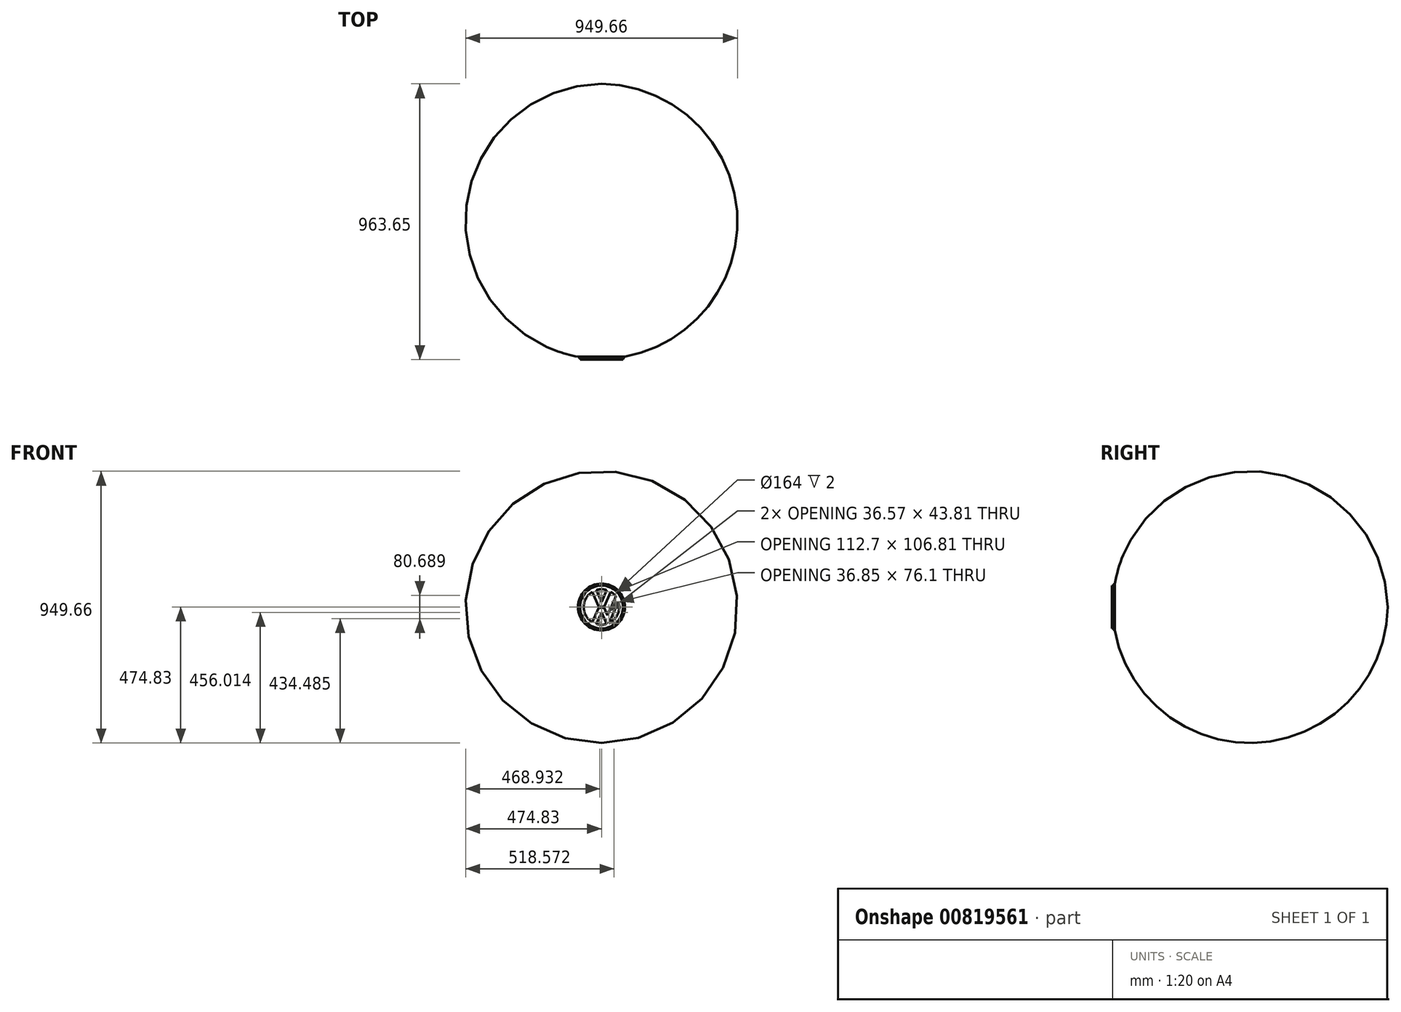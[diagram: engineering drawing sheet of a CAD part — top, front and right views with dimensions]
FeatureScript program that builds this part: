
annotation { "Feature Type Name" : "Feature", "Feature Type Description" : "" }
export const myFeature = defineFeature(function(context is Context, id is Id, definition is map)
    precondition{}
    {
        {
            var Q0;
            Q0=qCreatedBy(makeId("Front.planeOp"),FACE);
            var sketch = newSketch(context, id + "F0", { "sketchPlane" : qUnion([Q0])});
            skCircle(sketch, "E0", {"center": v(0, 0) * mm, "radius": 75 * mm});
            skCircle(sketch, "E1", {"center": v(0, 0) * mm, "radius": 62.25 * mm});
            skLineSegment(sketch, "E2", {"start": v(-31.99, 53.4) * mm, "end": v(18.28, -59.5) * mm});
            skLineSegment(sketch, "E3", {"start": v(31.99, 53.4) * mm, "end": v(-18.28, -59.5) * mm});
            skLineSegment(sketch, "E4", {"start": v(-18.28, 59.5) * mm, "end": v(31.99, -53.4) * mm});
            skLineSegment(sketch, "E5", {"start": v(18.28, 59.5) * mm, "end": v(-31.99, -53.4) * mm});
            skLineSegment(sketch, "E6", {"start": v(25.32, -56.87) * mm, "end": v(59.2, 19.24) * mm});
            skLineSegment(sketch, "E7", {"start": v(50.45, 36.46) * mm, "end": v(6.66, -61.9) * mm});
            skLineSegment(sketch, "E8", {"start": v(-25.32, -56.87) * mm, "end": v(-59.2, 19.24) * mm});
            skLineSegment(sketch, "E9", {"start": v(-50.45, 36.46) * mm, "end": v(-6.66, -61.9) * mm});
            skLineSegment(sketch, "E10", {"start": v(-9.04, 1.88) * mm, "end": v(9.04, 1.88) * mm});
            skLineSegment(sketch, "E11", {"start": v(-9.04, -1.88) * mm, "end": v(9.04, -1.88) * mm});
            skSolve(sketch);
        }
        {
            var Q0;
            {var subQ1=sQuery(id+"F0.wireOp",EDGE,"E1");var subQ7=sQuery(id+"F0.wireOp",EDGE,"E2");var subQ8=makeQuery(id+"F0.imprint","INTERSECT",VERTEX,{"disambiguationData":[OD(0.0)],"derivedFrom":[subQ1,subQ7]});Q0=makeQuery(id+"F0.imprint","IMPRINT",FACE,{"disambiguationData":[TD([[makeQuery(id+"F0.imprint","IMPRINT",EDGE,{"disambiguationData":[TD([[subQ8,1.0]])],"derivedFrom":subQ1}),1.0]])]});}
            var Q1;
            Q1=makeQuery(id+"F0.imprint","IMPRINT",FACE,{"disambiguationData":[TD([[makeQuery(id+"F0.imprint","IMPRINT",EDGE,{"derivedFrom":sQuery(id+"F0.wireOp",EDGE,"E0")}),1.0]])]});
            var Q2;
            {var subQ0=sQuery(id+"F0.wireOp",EDGE,"E8");var subQ1=sQuery(id+"F0.wireOp",EDGE,"E1");var subQ2=makeQuery(id+"F0.imprint","INTERSECT",VERTEX,{"disambiguationData":[OD(1.0)],"derivedFrom":[subQ1,subQ0]});Q2=makeQuery(id+"F0.imprint","IMPRINT",FACE,{"disambiguationData":[TD([[makeQuery(id+"F0.imprint","IMPRINT",EDGE,{"disambiguationData":[TD([[subQ2,1.0]])],"derivedFrom":subQ1}),1.0]])]});}
            var Q3;
            {var subQ5=sQuery(id+"F0.wireOp",EDGE,"E1");var subQ7=sQuery(id+"F0.wireOp",EDGE,"E3");var subQ8=makeQuery(id+"F0.imprint","INTERSECT",VERTEX,{"disambiguationData":[OD(1.0)],"derivedFrom":[subQ5,subQ7]});Q3=makeQuery(id+"F0.imprint","IMPRINT",FACE,{"disambiguationData":[TD([[makeQuery(id+"F0.imprint","IMPRINT",EDGE,{"disambiguationData":[TD([[subQ8,1.0]])],"derivedFrom":subQ5}),1.0]])]});}
            var Q4;
            {var subQ5=sQuery(id+"F0.wireOp",EDGE,"E11");var subQ7=sQuery(id+"F0.wireOp",EDGE,"E2");var subQ9=makeQuery(id+"F0.imprint","INTERSECT",VERTEX,{"derivedFrom":[subQ7,subQ5]});Q4=makeQuery(id+"F0.imprint","IMPRINT",FACE,{"disambiguationData":[TD([[makeQuery(id+"F0.imprint","IMPRINT",EDGE,{"disambiguationData":[TD([[subQ9,-1.0]])],"derivedFrom":subQ7}),-1.0]])]});}
            var Q5;
            {var subQ0=sQuery(id+"F0.wireOp",EDGE,"E11");var subQ1=sQuery(id+"F0.wireOp",EDGE,"E2");var subQ2=makeQuery(id+"F0.imprint","INTERSECT",VERTEX,{"derivedFrom":[subQ1,subQ0]});Q5=makeQuery(id+"F0.imprint","IMPRINT",FACE,{"disambiguationData":[TD([[makeQuery(id+"F0.imprint","IMPRINT",EDGE,{"disambiguationData":[TD([[subQ2,-1.0]])],"derivedFrom":subQ1}),1.0]])]});}
            var Q6;
            {var subQ0=sQuery(id+"F0.wireOp",EDGE,"E5");var subQ1=sQuery(id+"F0.wireOp",EDGE,"E4");var subQ2=makeQuery(id+"F0.imprint","INTERSECT",VERTEX,{"derivedFrom":[subQ1,subQ0]});Q6=makeQuery(id+"F0.imprint","IMPRINT",FACE,{"disambiguationData":[TD([[makeQuery(id+"F0.imprint","IMPRINT",EDGE,{"disambiguationData":[TD([[subQ2,-1.0]])],"derivedFrom":subQ1}),-1.0]])]});}
            var Q7;
            {var subQ1=sQuery(id+"F0.wireOp",EDGE,"E1");var subQ5=sQuery(id+"F0.wireOp",EDGE,"E3");var subQ6=makeQuery(id+"F0.imprint","INTERSECT",VERTEX,{"disambiguationData":[OD(0.0)],"derivedFrom":[subQ1,subQ5]});Q7=makeQuery(id+"F0.imprint","IMPRINT",FACE,{"disambiguationData":[TD([[makeQuery(id+"F0.imprint","IMPRINT",EDGE,{"disambiguationData":[TD([[subQ6,-1.0]])],"derivedFrom":subQ1}),1.0]])]});}
            var Q8;
            {var subQ5=sQuery(id+"F0.wireOp",EDGE,"E2");var subQ7=sQuery(id+"F0.wireOp",EDGE,"E3");var subQ8=makeQuery(id+"F0.imprint","INTERSECT",VERTEX,{"derivedFrom":[subQ5,subQ7]});Q8=makeQuery(id+"F0.imprint","IMPRINT",FACE,{"disambiguationData":[TD([[makeQuery(id+"F0.imprint","IMPRINT",EDGE,{"disambiguationData":[TD([[subQ8,-1.0]])],"derivedFrom":subQ5}),1.0]])]});}
            var Q9;
            {var subQ1=sQuery(id+"F0.wireOp",EDGE,"E1");var subQ5=sQuery(id+"F0.wireOp",EDGE,"E2");var subQ6=makeQuery(id+"F0.imprint","INTERSECT",VERTEX,{"disambiguationData":[OD(1.0)],"derivedFrom":[subQ1,subQ5]});Q9=makeQuery(id+"F0.imprint","IMPRINT",FACE,{"disambiguationData":[TD([[makeQuery(id+"F0.imprint","IMPRINT",EDGE,{"disambiguationData":[TD([[subQ6,-1.0]])],"derivedFrom":subQ1}),1.0]])]});}
            var Q10;
            {var subQ0=sQuery(id+"F0.wireOp",EDGE,"E6");var subQ1=sQuery(id+"F0.wireOp",EDGE,"E1");var subQ2=makeQuery(id+"F0.imprint","INTERSECT",VERTEX,{"disambiguationData":[OD(1.0)],"derivedFrom":[subQ1,subQ0]});Q10=makeQuery(id+"F0.imprint","IMPRINT",FACE,{"disambiguationData":[TD([[makeQuery(id+"F0.imprint","IMPRINT",EDGE,{"disambiguationData":[TD([[subQ2,-1.0]])],"derivedFrom":subQ1}),1.0]])]});}
            extrude(context, id + "F1", {"entities" : qUnion([Q0, Q1, Q2, Q3, Q4, Q5, Q6, Q7, Q8, Q9, Q10]), "depth" : 10 * mm, "offsetDistance" : 25 * mm});
        }
        {
            var Q0;
            Q0=qCreatedBy(makeId("Top.planeOp"),FACE);
            var sketch = newSketch(context, id + "F2", { "sketchPlane" : qUnion([Q0])});
            skLineSegment(sketch, "E12", {"start": v(0, 0) * mm, "end": v(0, -8) * mm});
            skLineSegment(sketch, "E13", {"start": v(0, 0) * mm, "end": v(-82, 0) * mm});
            skLineSegment(sketch, "E14", {"start": v(-82, 0) * mm, "end": v(-82, -2) * mm});
            skArc(sketch, "E15", {"start": v(-82, -2) * mm, "mid": v(-41.13, -6.76) * mm, "end": v(0, -8) * mm});
            skSolve(sketch);
        }
        {
            var Q0;
            Q0=makeQuery(id+"F2.imprint","IMPRINT",FACE,{"disambiguationData":[TD([[makeQuery(id+"F2.imprint","IMPRINT",EDGE,{"derivedFrom":sQuery(id+"F2.wireOp",EDGE,"E12")}),-1.0]])]});
            var Q1;
            Q1=sQuery(id+"F2.wireOp",EDGE,"E12");
            revolve(context, id + "F3", {"surfaceOperationType" : NewSurfaceOperationType.NEW, "entities" : qUnion([Q0]), "axis" : qUnion([Q1]), "revolveType" : RevolveType.FULL});
        }
    });
